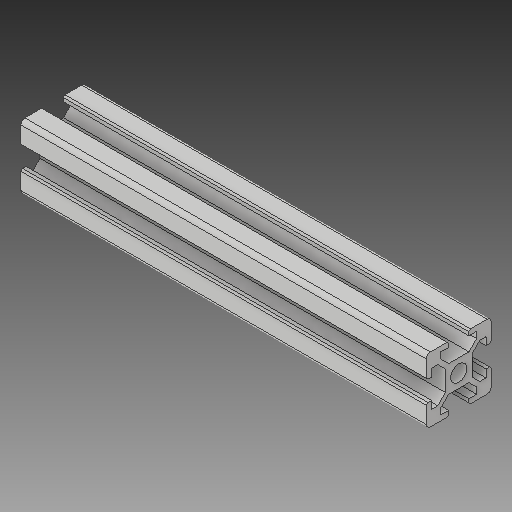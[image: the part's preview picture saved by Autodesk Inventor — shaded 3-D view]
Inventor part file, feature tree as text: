
AUTODESK INVENTOR PART (.ipt)
format: ipt  version: 2019 (Build 230136000, 136)  size: 183,808 bytes
history: native  units: in
note: dims shown in document units (in); Inventor stores cm internally (conversion verified against a paired STEP export)
features: extrude x1, fillet x1, sketch x1
ambient origin geometry x8: Origin, YZ Plane, XZ Plane, XY Plane, X Axis, Y Axis, Z Axis, Center Point
bodies: Solid1 (feature_tree)
feature tree (3):
  extrude  "Extrusion1"  Depth=0.0492in
  fillet  "Fillet1"  [1 undecoded]
  sketch  "Sketch1"  dims[d0=0.1969in d3=0.1417in d4=45.0deg d5=0.122in d7=0.2165in d8=0.063in d11=0.1693in d12=4.9213in d13=0.0in d14=0.0492in]
note: 1 required parameter value undecoded (feature->parameter linkage not recoverable at this tier; creation-order binding heuristic only, values carry confidence <= 0.55)
